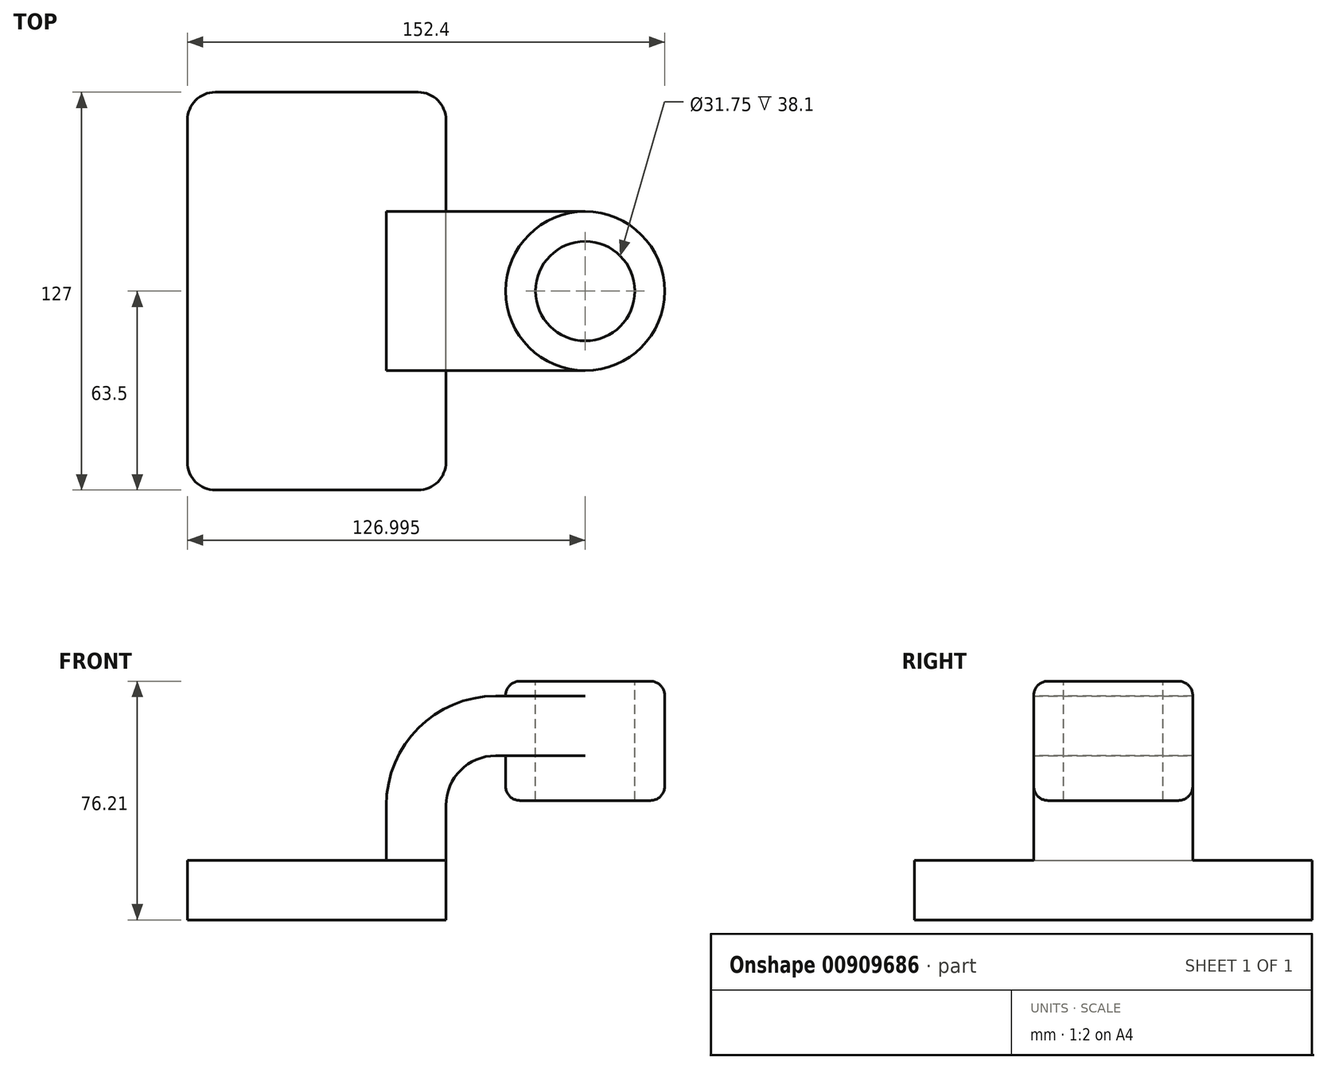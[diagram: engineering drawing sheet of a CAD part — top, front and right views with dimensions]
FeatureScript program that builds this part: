
annotation { "Feature Type Name" : "Feature", "Feature Type Description" : "" }
export const myFeature = defineFeature(function(context is Context, id is Id, definition is map)
    precondition{}
    {
        {
            var Q0;
            Q0=qCreatedBy(makeId("Front.planeOp"),FACE);
            var sketch = newSketch(context, id + "F0", { "sketchPlane" : qUnion([Q0])});
            skLineSegment(sketch, "E0.bottom", {"start": v(41.28, -9.52) * mm, "end": v(-41.27, -9.53) * mm});
            skLineSegment(sketch, "E0.top", {"start": v(41.27, 9.53) * mm, "end": v(-41.28, 9.53) * mm});
            skLineSegment(sketch, "E0.left", {"start": v(41.28, -9.52) * mm, "end": v(41.28, 9.53) * mm});
            skLineSegment(sketch, "E0.right", {"start": v(-41.27, -9.52) * mm, "end": v(-41.28, 9.53) * mm});
            skPoint(sketch, "E0.middle", {"position": v(0, 0) * mm});
            skLineSegment(sketch, "E1.bottom", {"start": v(111.12, 28.57) * mm, "end": v(60.32, 28.57) * mm});
            skLineSegment(sketch, "E1.top", {"start": v(111.12, 66.68) * mm, "end": v(60.32, 66.68) * mm});
            skLineSegment(sketch, "E1.left", {"start": v(111.12, 28.57) * mm, "end": v(111.12, 66.68) * mm});
            skLineSegment(sketch, "E1.right", {"start": v(60.32, 28.57) * mm, "end": v(60.32, 66.68) * mm});
            skPoint(sketch, "E1.middle", {"position": v(85.72, 47.63) * mm});
            skLineSegment(sketch, "E2", {"start": v(41.27, 9.53) * mm, "end": v(41.27, 27) * mm});
            skArc(sketch, "E3", {"start": v(41.27, 27) * mm, "mid": v(45.92, 38.23) * mm, "end": v(57.15, 42.88) * mm});
            skLineSegment(sketch, "E4", {"start": v(57.15, 42.88) * mm, "end": v(85.72, 42.88) * mm});
            skLineSegment(sketch, "E5.0", {"start": v(57.15, 61.93) * mm, "end": v(85.72, 61.93) * mm});
            skArc(sketch, "E5.1", {"start": v(22.23, 27) * mm, "mid": v(32.45, 51.7) * mm, "end": v(57.15, 61.93) * mm});
            skLineSegment(sketch, "E5.2", {"start": v(22.22, 9.53) * mm, "end": v(22.22, 27) * mm});
            skLineSegment(sketch, "E6", {"start": v(85.72, 28.57) * mm, "end": v(85.72, 66.68) * mm});
            skFitSpline(sketch, "E7", {"points": [v(-41.28, 9.53) * mm, v(57.15, 61.93) * mm], "startDerivative": vector(-1.15, 97.56) * mm, "endDerivative": vector(171.45, -95.95) * mm});
            skSolve(sketch);
        }
        {
            var Q0;
            Q0=makeQuery(id+"F0.imprint","IMPRINT",FACE,{"disambiguationData":[TD([[makeQuery(id+"F0.imprint","IMPRINT",EDGE,{"derivedFrom":sQuery(id+"F0.wireOp",EDGE,"E0.bottom")}),-1.0]])]});
            extrude(context, id + "F1", {"entities" : qUnion([Q0]), "endBound" : BoundingType.SYMMETRIC, "depth" : 127 * mm, "offsetDistance" : 25.4 * mm});
        }
        {
            var Q0;
            {var subQ1=sQuery(id+"F0.wireOp",EDGE,"E2");Q0=makeQuery(id+"F0.imprint","IMPRINT",FACE,{"disambiguationData":[TD([[makeQuery(id+"F0.imprint","IMPRINT",EDGE,{"derivedFrom":subQ1}),1.0]])]});}
            var Q1;
            {var subQ0=sQuery(id+"F0.wireOp",EDGE,"E4");var subQ1=sQuery(id+"F0.wireOp",EDGE,"E1.right");var subQ2=makeQuery(id+"F0.imprint","INTERSECT",VERTEX,{"derivedFrom":[subQ1,subQ0]});Q1=makeQuery(id+"F0.imprint","IMPRINT",FACE,{"disambiguationData":[TD([[makeQuery(id+"F0.imprint","IMPRINT",EDGE,{"disambiguationData":[TD([[subQ2,-1.0]])],"derivedFrom":subQ1}),-1.0]])]});}
            extrude(context, id + "F2", {"entities" : qUnion([Q0, Q1]), "operationType" : NewBodyOperationType.ADD, "endBound" : BoundingType.SYMMETRIC, "depth" : 50.8 * mm, "offsetDistance" : 25.4 * mm});
        }
        {
            var Q0;
            Q0=makeQuery(id+"F0.imprint","IMPRINT",FACE,{"disambiguationData":[TD([[makeQuery(id+"F0.imprint","IMPRINT",EDGE,{"derivedFrom":sQuery(id+"F0.wireOp",EDGE,"E5.1")}),1.0]])]});
            extrude(context, id + "F3", {"entities" : qUnion([Q0]), "operationType" : NewBodyOperationType.ADD, "endBound" : BoundingType.SYMMETRIC, "depth" : 15.88 * mm, "offsetDistance" : 25.4 * mm});
        }
        {
            var Q0;
            {var subQ4=sQuery(id+"F0.wireOp",EDGE,"E1.left");Q0=makeQuery(id+"F0.imprint","IMPRINT",FACE,{"disambiguationData":[TD([[makeQuery(id+"F0.imprint","IMPRINT",EDGE,{"derivedFrom":subQ4}),1.0]])]});}
            var Q1;
            Q1=sQuery(id+"F0.wireOp",EDGE,"E6");
            revolve(context, id + "F4", {"operationType" : NewBodyOperationType.ADD, "surfaceOperationType" : NewSurfaceOperationType.NEW, "entities" : qUnion([Q0]), "axis" : qUnion([Q1]), "revolveType" : RevolveType.FULL});
        }
        {
            var Q0;
            Q0=makeQuery(id+"F1.opExtrude","CAP_EDGE",EDGE,{"disambiguationData":[OSD([sQuery(id+"F0.wireOp",EDGE,"E0.right")])],"isStart":false});
            var Q1;
            Q1=makeQuery(id+"F1.opExtrude","CAP_EDGE",EDGE,{"disambiguationData":[OSD([sQuery(id+"F0.wireOp",EDGE,"E0.left")])],"isStart":false});
            var Q2;
            Q2=makeQuery(id+"F1.opExtrude","CAP_EDGE",EDGE,{"disambiguationData":[OSD([sQuery(id+"F0.wireOp",EDGE,"E0.left")])],"isStart":true});
            var Q3;
            Q3=makeQuery(id+"F1.opExtrude","CAP_EDGE",EDGE,{"disambiguationData":[OSD([sQuery(id+"F0.wireOp",EDGE,"E0.right")])],"isStart":true});
            fillet(context, id + "F5", {"entities" : qUnion([Q0, Q1, Q2, Q3]), "radius" : 8.9 * mm, "tangentPropagation" : true, "allowEdgeOverflow" : false});
        }
        {
            var Q0;
            Q0=makeQuery(id+"F4.opRevolve","SWEPT_FACE",FACE,{"disambiguationData":[OSD([sQuery(id+"F0.wireOp",EDGE,"E1.top")])]});
            var sketch = newSketch(context, id + "F6", { "sketchPlane" : qUnion([Q0])});
            skCircle(sketch, "E8", {"center": v(85.72, 0) * mm, "radius": 15.88 * mm});
            skSolve(sketch);
        }
        {
            var Q0;
            Q0 = qSketchRegion(id + "F6", true);
            var Q1;
            Q1=makeQuery(id+"F4.opRevolve","SWEPT_FACE",FACE,{"disambiguationData":[OSD([sQuery(id+"F0.wireOp",EDGE,"E1.bottom")])]});
            extrude(context, id + "F7", {"entities" : qUnion([Q0]), "operationType" : NewBodyOperationType.REMOVE, "endBound" : BoundingType.UP_TO_SURFACE, "oppositeDirection" : true, "depth" : 64.26 * mm, "endBoundEntityFace" : qUnion([Q1]), "offsetDistance" : 25.4 * mm});
        }
        {
            var Q0;
            Q0=makeQuery(id+"F7.boolean.opBoolean","COPY",EDGE,{"derivedFrom":makeQuery(id+"F7.opExtrude","CAP_EDGE",EDGE,{"disambiguationData":[OSD([sQuery(id+"F6.wireOp",EDGE,"E8")])],"isStart":true})});
            var Q1;
            Q1=makeQuery(id+"F7.boolean.opBoolean","COPY",EDGE,{"derivedFrom":makeQuery(id+"F7.opExtrude","CAP_EDGE",EDGE,{"disambiguationData":[OSD([sQuery(id+"F6.wireOp",EDGE,"E8")])],"isStart":false})});
            var Q2;
            Q2=makeQuery(id+"F4.opRevolve","SWEPT_EDGE",EDGE,{"disambiguationData":[OSD([sQuery(id+"F0.wireOp",EDGE,"E1.top"),sQuery(id+"F0.wireOp",EDGE,"E1.left")])]});
            var Q3;
            Q3=makeQuery(id+"F4.opRevolve","SWEPT_EDGE",EDGE,{"disambiguationData":[OSD([sQuery(id+"F0.wireOp",EDGE,"E1.bottom"),sQuery(id+"F0.wireOp",EDGE,"E1.left")])]});
            fillet(context, id + "F8", {"entities" : qUnion([Q0, Q1, Q2, Q3]), "radius" : 4.57 * mm, "tangentPropagation" : true, "allowEdgeOverflow" : false});
        }
    });
